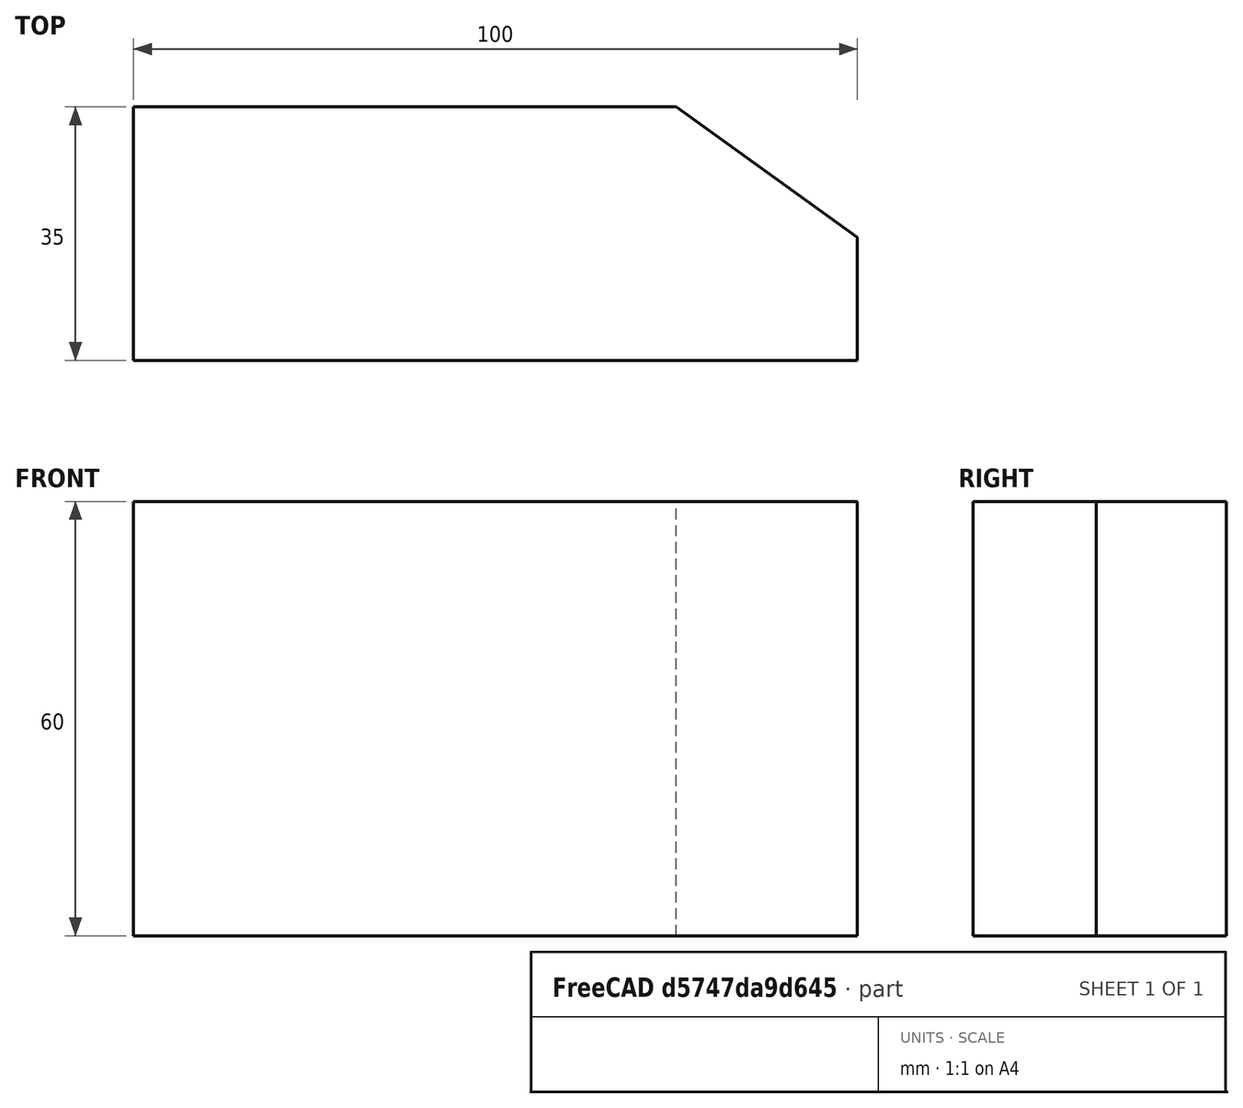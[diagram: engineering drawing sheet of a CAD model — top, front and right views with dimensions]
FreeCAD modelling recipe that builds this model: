
FCSTD DOCUMENT  (FreeCAD 0.18.4R)
Label: car-body
License: All rights reserved
LicenseURL: http://en.wikipedia.org/wiki/All_rights_reserved
objects: Sketcher::SketchObject×1, PartDesign::Pad×1, PartDesign::Body×1
note: 4 computed .brp shape members not serialized (recipe doc carries the construction recipe); baked Part::Feature solids carry a one-line shape summary decoded from their .brp

FEATURE [Sketcher::SketchObject] Sketch
  MapMode = 5
  Support = -> [XY_Plane]
  sketch-geometry (5):
    g0: LineSegment StartX=0 StartY=0 StartZ=0 EndX=-100 EndY=0 EndZ=0
    g1: LineSegment StartX=-100 StartY=0 StartZ=0 EndX=-100 EndY=35 EndZ=0
    g2: LineSegment StartX=-100 StartY=35 StartZ=0 EndX=-25 EndY=35 EndZ=0
    g3: LineSegment StartX=0 StartY=17 StartZ=0 EndX=0 EndY=0 EndZ=0
    g4: LineSegment StartX=0 StartY=17 StartZ=0 EndX=-25 EndY=35 EndZ=0
  constraints (14):
    c: Coincident(g0,g1)
    c: Coincident(g1,g2)
    c: Coincident(g3,g0)
    c: Horizontal(g0)
    c: Horizontal(g2)
    c: Vertical(g1)
    c: Vertical(g3)
    c: Coincident(g0,g-1)
    c: DistanceY(g1,g1) = 35
    c: DistanceX(g0,g0) = 100
    c: Coincident(g3,g4)
    c: DistanceY(g3,g3) = 17
    c: Coincident(g4,g2)
    c: DistanceX(g4,g4) = 25
FEATURE [PartDesign::Pad] Pad
  Length = 60
  Length2 = 100
  Midplane = true
  Profile = -> Sketch
  Type = 0
FEATURE [PartDesign::Body] Body
  Group = -> [Sketch,Pad]
  Origin = -> Origin
  Tip = -> Pad
